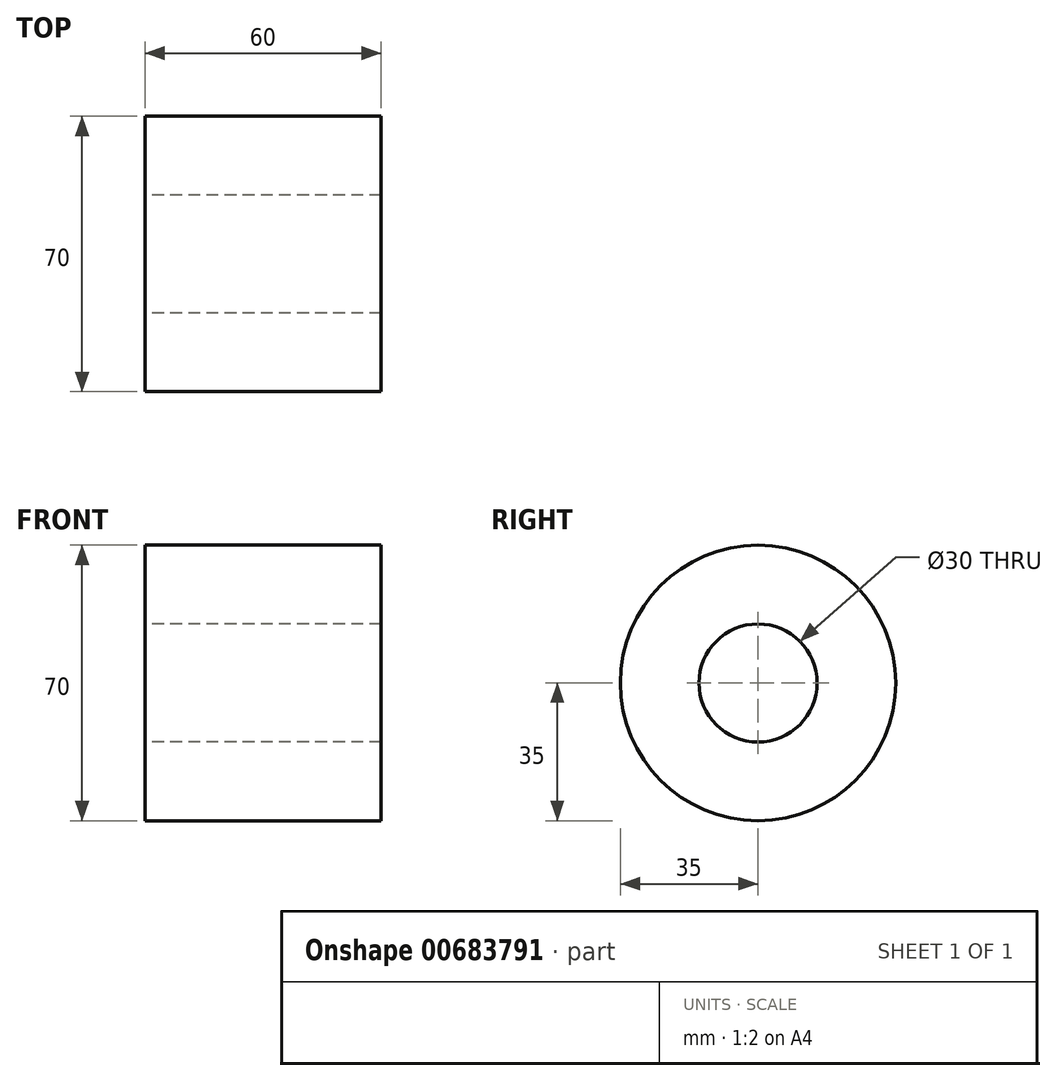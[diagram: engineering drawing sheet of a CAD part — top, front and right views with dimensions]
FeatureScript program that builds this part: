
annotation { "Feature Type Name" : "Feature", "Feature Type Description" : "" }
export const myFeature = defineFeature(function(context is Context, id is Id, definition is map)
    precondition{}
    {
        {
            var Q0;
            Q0=qCreatedBy(makeId("Right.planeOp"),FACE);
            var sketch = newSketch(context, id + "F0", { "sketchPlane" : qUnion([Q0])});
            skCircle(sketch, "E0", {"center": v(0, 0) * mm, "radius": 35 * mm});
            skCircle(sketch, "E1", {"center": v(0, 0) * mm, "radius": 15 * mm});
            skSolve(sketch);
        }
        {
            var Q0;
            Q0=makeQuery(id+"F0.imprint","IMPRINT",FACE,{"disambiguationData":[TD([[makeQuery(id+"F0.imprint","IMPRINT",EDGE,{"derivedFrom":sQuery(id+"F0.wireOp",EDGE,"E0")}),1.0]])]});
            extrude(context, id + "F1", {"entities" : qUnion([Q0]), "depth" : 60 * mm, "offsetDistance" : 25 * mm});
        }
    });
